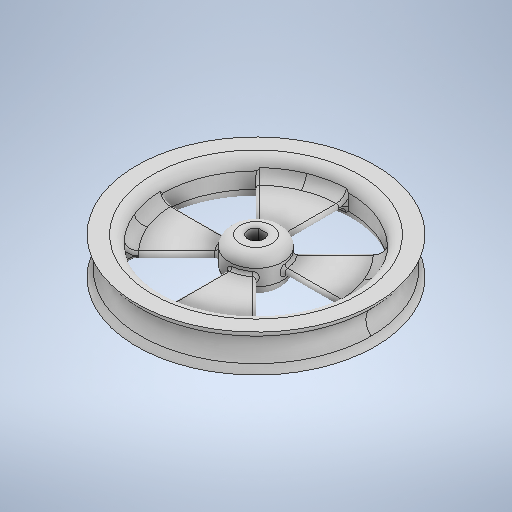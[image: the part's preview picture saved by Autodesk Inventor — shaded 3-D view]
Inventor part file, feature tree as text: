
AUTODESK INVENTOR PART (.ipt)
format: ipt  version: 2025.2 (Build 292293000, 293)  size: 1,091,584 bytes
history: native  units: mm
features: extrude x7, sketch x6, fillet x5, other x1
ambient origin geometry x8: Origin, YZ Plane, XZ Plane, XY Plane, X Axis, Y Axis, Z Axis, Center Point
bodies: Body1 (feature_tree)
feature tree (19):
  other  "Sólido1"
  extrude  "Extrusão1"  Depth=2.0mm TaperAngle=0.0deg
  extrude  "Extrusão2"  Depth=3.0mm TaperAngle=0.0deg
  extrude  "Extrusão3"  Depth=3.0mm
  fillet  "Arredondamento1"  [1 undecoded]
  sketch  "Esboço4"  dims[d15=135.0deg d16=135.0deg]
  extrude  "Extrusão4"  TaperAngle=135.0deg  [1 undecoded]
  extrude  "Extrusão5"  Depth=3.0mm TaperAngle=0.0deg
  extrude  "Extrusão6"  Depth=0.5mm TaperAngle=0.0deg
  fillet  "Arredondamento2"  Radius=2.0mm
  fillet  "Arredondamento3"  Radius=2.0mm
  fillet  "Arredondamento4"  Radius=0.5mm
  extrude  "Extrusão7"  Depth=0.5mm
  fillet  "Arredondamento5"  Radius=2.5mm
  sketch  "Esboço1"  dims[d0=45.0mm d1=2.0mm d2=0.0mm]
  sketch  "Esboço2"  dims[d3=40.0mm d4=3.0mm d5=0.0mm]
  sketch  "Esboço3"  dims[d6=2.0mm d7=0.0mm d8=3.0mm d14=45.0deg]
  sketch  "Esboço5"  dims[d17=10.0mm d18=0.0mm d19=3.0mm d20=0.0mm]
  sketch  "Esboço6"  dims[d21=90.0deg d22=3.0mm d23=0.0mm d24=2.0mm d25=2.0mm d26=0.5mm d27=3.0mm d28=2.5mm d29=0.0mm d30=0.0mm d31=0.5mm]
note: 2 required parameter values undecoded (feature->parameter linkage not recoverable at this tier; creation-order binding heuristic only, values carry confidence <= 0.55)
